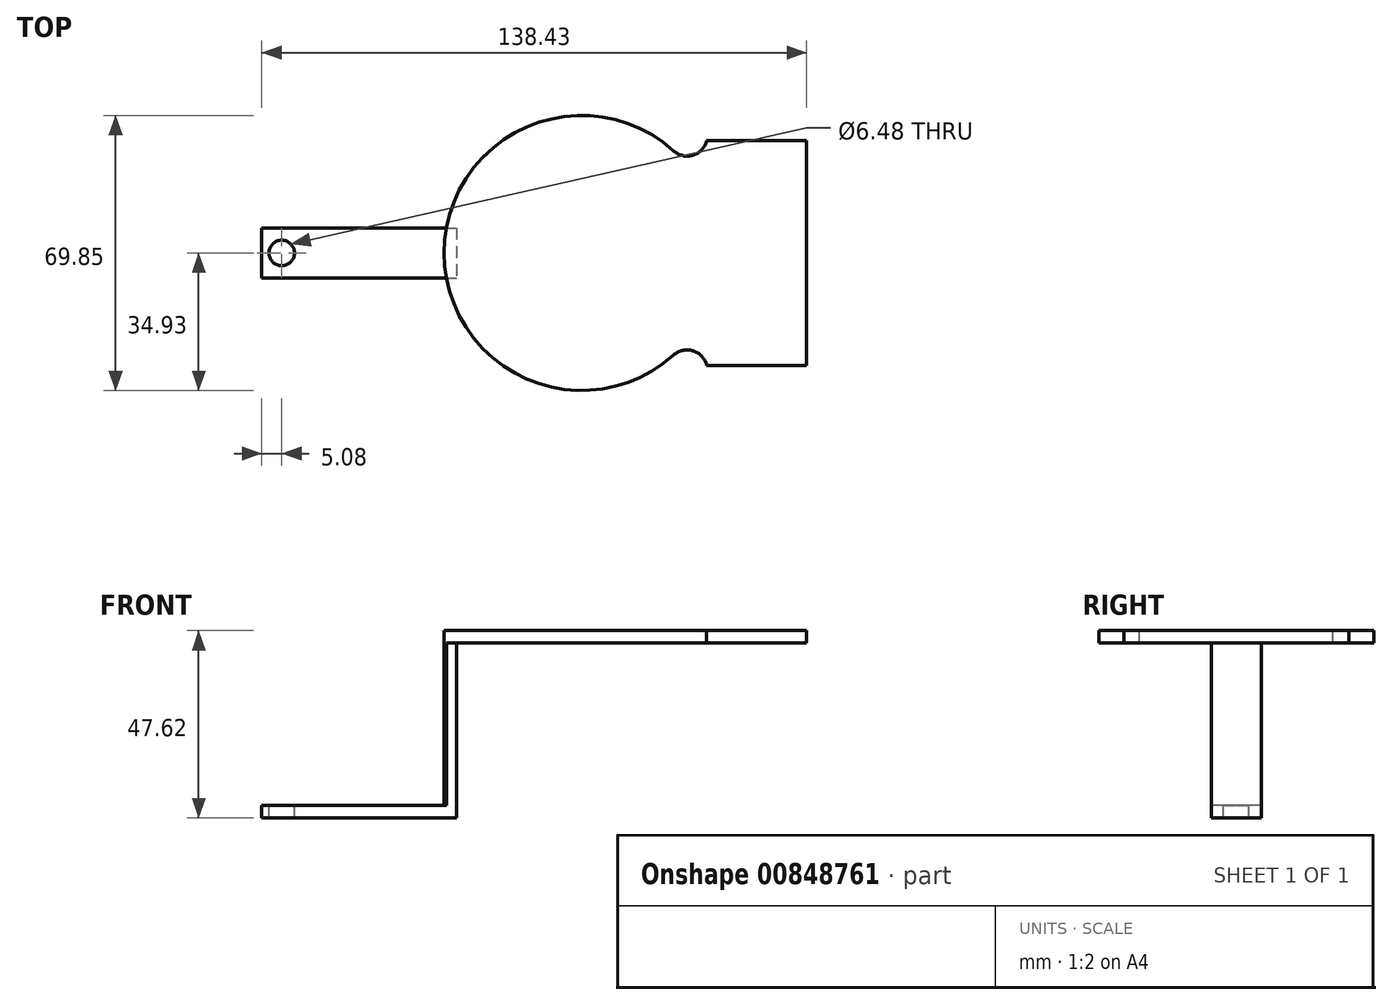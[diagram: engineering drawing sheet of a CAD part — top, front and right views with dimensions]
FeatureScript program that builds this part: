
annotation { "Feature Type Name" : "Feature", "Feature Type Description" : "" }
export const myFeature = defineFeature(function(context is Context, id is Id, definition is map)
    precondition{}
    {
        {
            var Q0;
            Q0=qCreatedBy(makeId("Front.planeOp"),FACE);
            var sketch = newSketch(context, id + "F0", { "sketchPlane" : qUnion([Q0])});
            skLineSegment(sketch, "E0", {"start": v(0, 0) * mm, "end": v(0, 76.2) * mm});
            skSolve(sketch);
        }
        {
            var Q0;
            Q0=qCreatedBy(makeId("Top.planeOp"),FACE);
            var sketch = newSketch(context, id + "F1", { "sketchPlane" : qUnion([Q0])});
            skCircle(sketch, "E1", {"center": v(0, 0) * mm, "radius": 76.2 * mm, "construction": true});
            skCircle(sketch, "E2", {"center": v(0, 0) * mm, "radius": 34.93 * mm});
            skLineSegment(sketch, "E3.bottom", {"start": v(31.75, 28.57) * mm, "end": v(57.15, 28.57) * mm});
            skLineSegment(sketch, "E3.top", {"start": v(31.75, -28.58) * mm, "end": v(57.15, -28.58) * mm});
            skLineSegment(sketch, "E3.left", {"start": v(31.75, 28.58) * mm, "end": v(31.75, -28.57) * mm});
            skLineSegment(sketch, "E3.right", {"start": v(57.15, 28.58) * mm, "end": v(57.15, -28.57) * mm});
            skLineSegment(sketch, "E4.bottom", {"start": v(-25.4, 57.15) * mm, "end": v(25.4, 57.15) * mm, "construction": true});
            skLineSegment(sketch, "E4.top", {"start": v(-25.4, 31.75) * mm, "end": v(25.4, 31.75) * mm, "construction": true});
            skLineSegment(sketch, "E4.left", {"start": v(-25.4, 57.15) * mm, "end": v(-25.4, 31.75) * mm, "construction": true});
            skLineSegment(sketch, "E4.right", {"start": v(25.4, 57.15) * mm, "end": v(25.4, 31.75) * mm, "construction": true});
            skLineSegment(sketch, "E5", {"start": v(0, 57.15) * mm, "end": v(0, 0) * mm, "construction": true});
            skLineSegment(sketch, "E6", {"start": v(57.15, 0) * mm, "end": v(0, 0) * mm, "construction": true});
            skCircle(sketch, "E7", {"center": v(-76.2, 0) * mm, "radius": 3.24 * mm});
            skCircle(sketch, "E8", {"center": v(76.2, 0) * mm, "radius": 3.24 * mm});
            skCircle(sketch, "E9", {"center": v(0, 76.2) * mm, "radius": 3.24 * mm});
            skCircle(sketch, "E10", {"center": v(0, -76.2) * mm, "radius": 3.24 * mm});
            skLineSegment(sketch, "E11.bottom", {"start": v(-81.28, 6.35) * mm, "end": v(-31.75, 6.35) * mm});
            skLineSegment(sketch, "E11.top", {"start": v(-81.28, -6.35) * mm, "end": v(-31.75, -6.35) * mm});
            skLineSegment(sketch, "E11.left", {"start": v(-81.28, 6.35) * mm, "end": v(-81.28, -6.35) * mm});
            skLineSegment(sketch, "E11.right", {"start": v(-31.75, 6.35) * mm, "end": v(-31.75, -6.35) * mm});
            skLineSegment(sketch, "E12", {"start": v(-31.75, 0) * mm, "end": v(0, 0) * mm, "construction": true});
            skSolve(sketch);
        }
        {
            var Q0;
            Q0=makeQuery(id+"F1.imprint","IMPRINT",FACE,{"disambiguationData":[TD([[makeQuery(id+"F1.imprint","IMPRINT",EDGE,{"derivedFrom":sQuery(id+"F1.wireOp",EDGE,"E7")}),-1.0]])]});
            var Q1;
            {var subQ5=sQuery(id+"F1.wireOp",EDGE,"E11.right");Q1=makeQuery(id+"F1.imprint","IMPRINT",FACE,{"disambiguationData":[TD([[makeQuery(id+"F1.imprint","IMPRINT",EDGE,{"derivedFrom":subQ5}),-1.0]])]});}
            extrude(context, id + "F2", {"entities" : qUnion([Q0, Q1]), "oppositeDirection" : true, "depth" : 44.45 * mm, "offsetDistance" : 25.4 * mm});
        }
        {
            var Q0;
            Q0=makeQuery(id+"F1.imprint","IMPRINT",FACE,{"disambiguationData":[TD([[makeQuery(id+"F1.imprint","IMPRINT",EDGE,{"derivedFrom":sQuery(id+"F1.wireOp",EDGE,"E7")}),-1.0]])]});
            extrude(context, id + "F3", {"entities" : qUnion([Q0]), "operationType" : NewBodyOperationType.REMOVE, "oppositeDirection" : true, "depth" : 41.27 * mm, "offsetDistance" : 25.4 * mm});
        }
        {
            var Q0;
            {var subQ6=sQuery(id+"F1.wireOp",EDGE,"E11.right");Q0=makeQuery(id+"F1.imprint","IMPRINT",FACE,{"disambiguationData":[TD([[makeQuery(id+"F1.imprint","IMPRINT",EDGE,{"derivedFrom":subQ6}),1.0]])]});}
            var Q1;
            {var subQ5=sQuery(id+"F1.wireOp",EDGE,"E11.right");Q1=makeQuery(id+"F1.imprint","IMPRINT",FACE,{"disambiguationData":[TD([[makeQuery(id+"F1.imprint","IMPRINT",EDGE,{"derivedFrom":subQ5}),-1.0]])]});}
            var Q2;
            {var subQ1=sQuery(id+"F1.wireOp",EDGE,"E3.bottom");Q2=makeQuery(id+"F1.imprint","IMPRINT",FACE,{"disambiguationData":[TD([[makeQuery(id+"F1.imprint","IMPRINT",EDGE,{"derivedFrom":subQ1}),-1.0]])]});}
            var Q3;
            {var subQ0=sQuery(id+"F1.wireOp",EDGE,"E3.left");var subQ1=sQuery(id+"F1.wireOp",EDGE,"E2");var subQ2=makeQuery(id+"F1.imprint","INTERSECT",VERTEX,{"disambiguationData":[OD(0.0)],"derivedFrom":[subQ1,subQ0]});Q3=makeQuery(id+"F1.imprint","IMPRINT",FACE,{"disambiguationData":[TD([[makeQuery(id+"F1.imprint","IMPRINT",EDGE,{"disambiguationData":[TD([[subQ2,1.0]])],"derivedFrom":subQ1}),1.0]])]});}
            extrude(context, id + "F4", {"entities" : qUnion([Q0, Q1, Q2, Q3]), "operationType" : NewBodyOperationType.ADD, "depth" : 3.17 * mm, "offsetDistance" : 25.4 * mm});
        }
        {
            var Q0;
            {var subQ0=sQuery(id+"F1.wireOp",EDGE,"E3.left");var subQ1=sQuery(id+"F1.wireOp",EDGE,"E2");Q0=makeQuery(id+"F4.opExtrude","SWEPT_EDGE",EDGE,{"disambiguationData":[OSD([subQ1,subQ0]),TDD([makeQuery(id+"F1.imprint","INTERSECT",VERTEX,{"disambiguationData":[OD(1.0)],"derivedFrom":[subQ1,subQ0]})])]});}
            var Q1;
            {var subQ0=sQuery(id+"F1.wireOp",EDGE,"E3.left");var subQ1=sQuery(id+"F1.wireOp",EDGE,"E2");Q1=makeQuery(id+"F4.opExtrude","SWEPT_EDGE",EDGE,{"disambiguationData":[OSD([subQ1,subQ0]),TDD([makeQuery(id+"F1.imprint","INTERSECT",VERTEX,{"disambiguationData":[OD(0.0)],"derivedFrom":[subQ1,subQ0]})])]});}
            var Q2;
            Q2=makeQuery(id+"FAkAuQthRJEk25y_2.2.F3.boolean.opBoolean","COPY",EDGE,{"derivedFrom":makeQuery(id+"FAkAuQthRJEk25y_2.2.F3.opExtrude","SWEPT_EDGE",EDGE,{"disambiguationData":[OSD([sQuery(id+"F1.wireOp",EDGE,"E2"),sQuery(id+"F1.wireOp",EDGE,"E11.top")])]})});
            fillet(context, id + "F5", {"entities" : qUnion([Q0, Q1, Q2]), "radius" : 5.08 * mm, "tangentPropagation" : true, "allowEdgeOverflow" : false});
        }
    });
